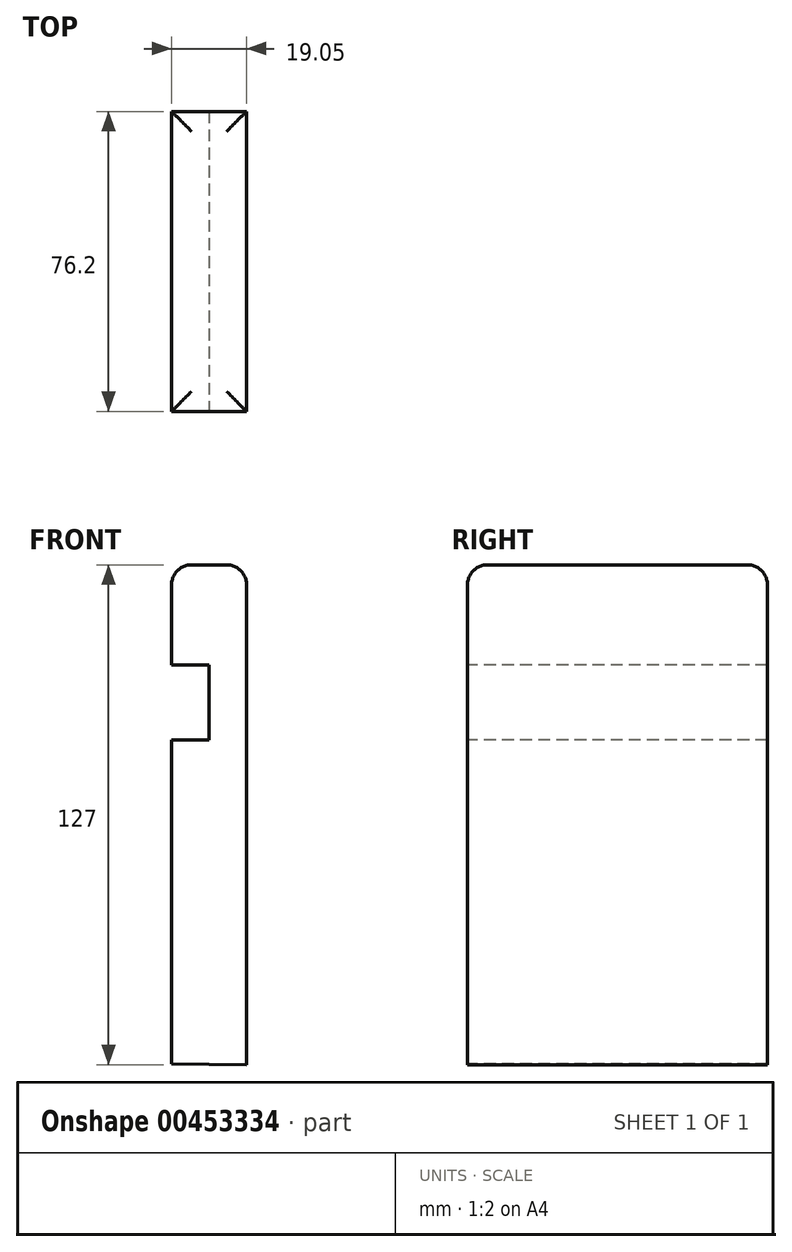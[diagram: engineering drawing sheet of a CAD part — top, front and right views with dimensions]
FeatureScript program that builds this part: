
annotation { "Feature Type Name" : "Feature", "Feature Type Description" : "" }
export const myFeature = defineFeature(function(context is Context, id is Id, definition is map)
    precondition{}
    {
        {
            var Q0;
            Q0=qCreatedBy(makeId("Front.planeOp"),FACE);
            var sketch = newSketch(context, id + "F0", { "sketchPlane" : qUnion([Q0])});
            skLineSegment(sketch, "E0", {"start": v(30.12, -65.1) * mm, "end": v(30.12, 61.9) * mm});
            skLineSegment(sketch, "E1", {"start": v(30.12, 61.9) * mm, "end": v(11.07, 61.9) * mm});
            skLineSegment(sketch, "E2", {"start": v(11.07, 61.9) * mm, "end": v(11.07, 36.5) * mm});
            skLineSegment(sketch, "E3", {"start": v(11.07, 36.5) * mm, "end": v(20.6, 36.5) * mm});
            skLineSegment(sketch, "E4", {"start": v(20.6, 36.5) * mm, "end": v(20.6, 17.46) * mm});
            skLineSegment(sketch, "E5", {"start": v(20.6, 17.46) * mm, "end": v(11.07, 17.46) * mm});
            skLineSegment(sketch, "E6", {"start": v(11.07, 17.46) * mm, "end": v(11.07, -64.86) * mm});
            skLineSegment(sketch, "E7", {"start": v(11.07, -64.86) * mm, "end": v(30.12, -65.1) * mm});
            skSolve(sketch);
        }
        {
            var Q0;
            Q0 = qSketchRegion(id + "F0", true);
            extrude(context, id + "F1", {"entities" : qUnion([Q0]), "oppositeDirection" : true, "depth" : 76.2 * mm});
        }
        {
            var Q0;
            Q0=makeQuery(id+"F1.opExtrude","CAP_EDGE",EDGE,{"disambiguationData":[OSD([sQuery(id+"F0.wireOp",EDGE,"E1")])],"isStart":false});
            var Q1;
            Q1=makeQuery(id+"F1.opExtrude","SWEPT_EDGE",EDGE,{"disambiguationData":[OSD([sQuery(id+"F0.wireOp",EDGE,"E0"),sQuery(id+"F0.wireOp",EDGE,"E1")])]});
            var Q2;
            Q2=makeQuery(id+"F1.opExtrude","CAP_EDGE",EDGE,{"disambiguationData":[OSD([sQuery(id+"F0.wireOp",EDGE,"E1")])],"isStart":true});
            var Q3;
            Q3=makeQuery(id+"F1.opExtrude","SWEPT_EDGE",EDGE,{"disambiguationData":[OSD([sQuery(id+"F0.wireOp",EDGE,"E1"),sQuery(id+"F0.wireOp",EDGE,"E2")])]});
            fillet(context, id + "F2", {"entities" : qUnion([Q0, Q1, Q2, Q3]), "radius" : 5.08 * mm, "tangentPropagation" : true, "allowEdgeOverflow" : false});
        }
    });
